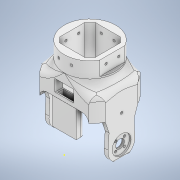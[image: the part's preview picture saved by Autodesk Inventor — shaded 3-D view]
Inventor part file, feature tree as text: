
AUTODESK INVENTOR PART (.ipt)
format: ipt  version: 2021 (Build 250183000, 183)  size: 820,224 bytes
history: native  units: mm
features: sketch x31, extrude x29, fillet x13, other x1, chamfer x1
ambient origin geometry x8: Origin, YZ Plane, XZ Plane, XY Plane, X Axis, Y Axis, Z Axis, Center Point
bodies: Body1 (feature_tree)
feature tree (75):
  other  "Sólido1"
  extrude  "Extrusión1"  Depth=8.0mm
  extrude  "Extrusión2"  Depth=400.0mm TaperAngle=0.0deg
  extrude  "Extrusión3"  Depth=40.0mm TaperAngle=0.0deg
  extrude  "Extrusión4"  Depth=12.0mm TaperAngle=0.0deg
  extrude  "Extrusión5"  Depth=160.0mm TaperAngle=0.0deg
  extrude  "Extrusión7"  Depth=2.0mm
  extrude  "Extrusión8"  Depth=50.0mm TaperAngle=0.0deg
  extrude  "Extrusión9"  Depth=10.0mm
  fillet  "Empalme2"  Radius=10.0mm
  fillet  "Empalme3"  Radius=10.0mm
  extrude  "Extrusión10"  Depth=10.0mm
  extrude  "Extrusión11"  Depth=10.0mm
  fillet  "Empalme4"  Radius=3.0mm
  fillet  "Empalme5"  Radius=500.0mm
  fillet  "Empalme6"  Radius=3.0mm
  fillet  "Empalme7"  Radius=3.0mm
  fillet  "Empalme8"  Radius=500.0mm
  fillet  "Empalme9"  Radius=0.1mm
  fillet  "Empalme10"  Radius=100.0mm
  extrude  "Extrusión12"  Depth=30.0mm
  extrude  "Extrusión13"  Depth=60.0mm TaperAngle=0.0deg
  fillet  "Empalme12"  Radius=6.0mm
  extrude  "Extrusión17"  Depth=2.0mm
  extrude  "Extrusión22"  Depth=15.0mm
  extrude  "Extrusión23"  Depth=3.0mm
  sketch  "Boceto34"  dims[d180=12.0mm d181=0.0mm d182=20.0mm d183=0.0mm]
  extrude  "Extrusión26"  Depth=20.0mm TaperAngle=0.0deg
  extrude  "Extrusión31"  Depth=7.4mm TaperAngle=0.0deg
  extrude  "Extrusión32"  Depth=900.0mm TaperAngle=0.0deg
  sketch  "Boceto43"  dims[d248=24.0mm d249=2.0mm d250=0.0mm]
  extrude  "Extrusión35"  Depth=2.0mm TaperAngle=0.0deg
  extrude  "Extrusión36"  Depth=2.0mm TaperAngle=0.0deg
  extrude  "Extrusión37"  Depth=3.0mm
  extrude  "Extrusión46"  Depth=1000.0mm TaperAngle=0.0deg
  extrude  "Extrusión47"  Depth=10.0mm TaperAngle=45.0deg
  extrude  "Extrusión48"  Depth=50.0mm TaperAngle=0.0deg
  extrude  "Extrusión50"  Depth=3.0mm
  extrude  "Extrusión51"  Depth=2.0mm
  extrude  "Extrusión52"  Depth=0.872665mm
  chamfer  "Chaflán1"  Distance=0.5mm
  fillet  "Empalme22"  Radius=0.872665mm
  extrude  "Extrusión53"  Depth=0.5mm
  fillet  "Empalme23"  Radius=0.872665mm
  extrude  "Extrusión54"  Depth=0.5mm
  fillet  "Empalme24"  Radius=0.872665mm
  sketch  "Boceto1"  dims[d7=40.0mm d8=0.0mm d10=8.0mm]
  sketch  "Boceto2"  dims[d11=400.0mm d12=0.0mm d16=400.0mm d17=0.0mm]
  sketch  "Boceto3"  dims[d18=400.0mm d19=0.0mm d20=40.0mm d21=0.0mm]
  sketch  "Boceto4"  dims[d25=62.249mm d26=0.0mm d27=12.0mm d28=0.0mm]
  sketch  "Boceto5"  dims[d32=9.0mm d37=160.0mm d38=0.0mm]
  sketch  "Boceto8"  dims[d39=2.0mm d40=2.0mm]
  sketch  "Boceto9"  dims[d47=160.0mm d48=0.0mm d49=50.0mm d50=0.0mm]
  sketch  "Boceto13"  dims[d51=10.0mm d52=10.0mm d53=10.0mm d54=10.0mm]
  sketch  "Boceto15"  dims[d55=10.0mm d56=10.0mm]
  sketch  "Boceto16"  dims[d57=10.0mm d62=3.0mm d63=3.0mm d64=500.0mm d65=0.0mm d70=3.0mm d71=3.0mm d72=500.0mm d73=0.0mm d94=0.1mm d106=100.0mm d107=0.0mm]
  sketch  "Boceto17"  dims[d130=16.0mm d133=30.0mm]
  sketch  "Boceto18"  dims[d134=40.0mm d135=0.0mm d142=60.0mm d143=0.0mm d157=6.0mm d158=0.0mm]
  sketch  "Boceto23"  dims[d174=2.0mm d175=15.0mm]
  sketch  "Boceto30"  dims[d176=24.0mm d177=15.0mm]
  sketch  "Boceto31"  dims[d178=5.0mm d179=3.0mm]
  sketch  "Boceto35"  dims[d201=7.4mm d202=0.0mm d203=7.4mm d204=0.0mm]
  sketch  "Boceto41"  dims[d205=18.0mm d206=0.0mm d243=900.0mm d244=0.0mm]
  sketch  "Boceto42"  dims[d245=24.0mm d246=2.0mm d247=0.0mm]
  sketch  "Boceto47"  dims[d258=3.0mm d259=3.0mm]
  sketch  "Boceto48"  dims[d260=1000.0mm d261=0.0mm d267=1000.0mm d268=0.0mm]
  sketch  "Boceto49"  dims[d269=50.0mm d270=0.0mm d271=10.0mm d272=2.0mm d273=45.0deg]
  sketch  "Boceto60"  dims[d274=4.0mm d277=50.0mm d278=0.0mm]
  sketch  "Boceto61"  dims[d279=6.0mm d280=3.0mm]
  sketch  "Boceto62"  dims[d281=200.0mm d282=0.0mm d283=2.0mm]
  sketch  "Boceto64"  dims[d108=0.5mm d109=0.872665mm]
  sketch  "Boceto65"  dims[d172=0.5mm]
  sketch  "Boceto66"  dims[d173=0.872665mm]
  sketch  "Boceto67"  dims[d207=0.5mm]
  sketch  "Boceto68"  dims[d208=0.872665mm d216=0.5mm d217=0.872665mm d218=0.5mm d219=0.872665mm d251=0.5mm d252=0.872665mm d253=0.5mm d254=0.872665mm]
